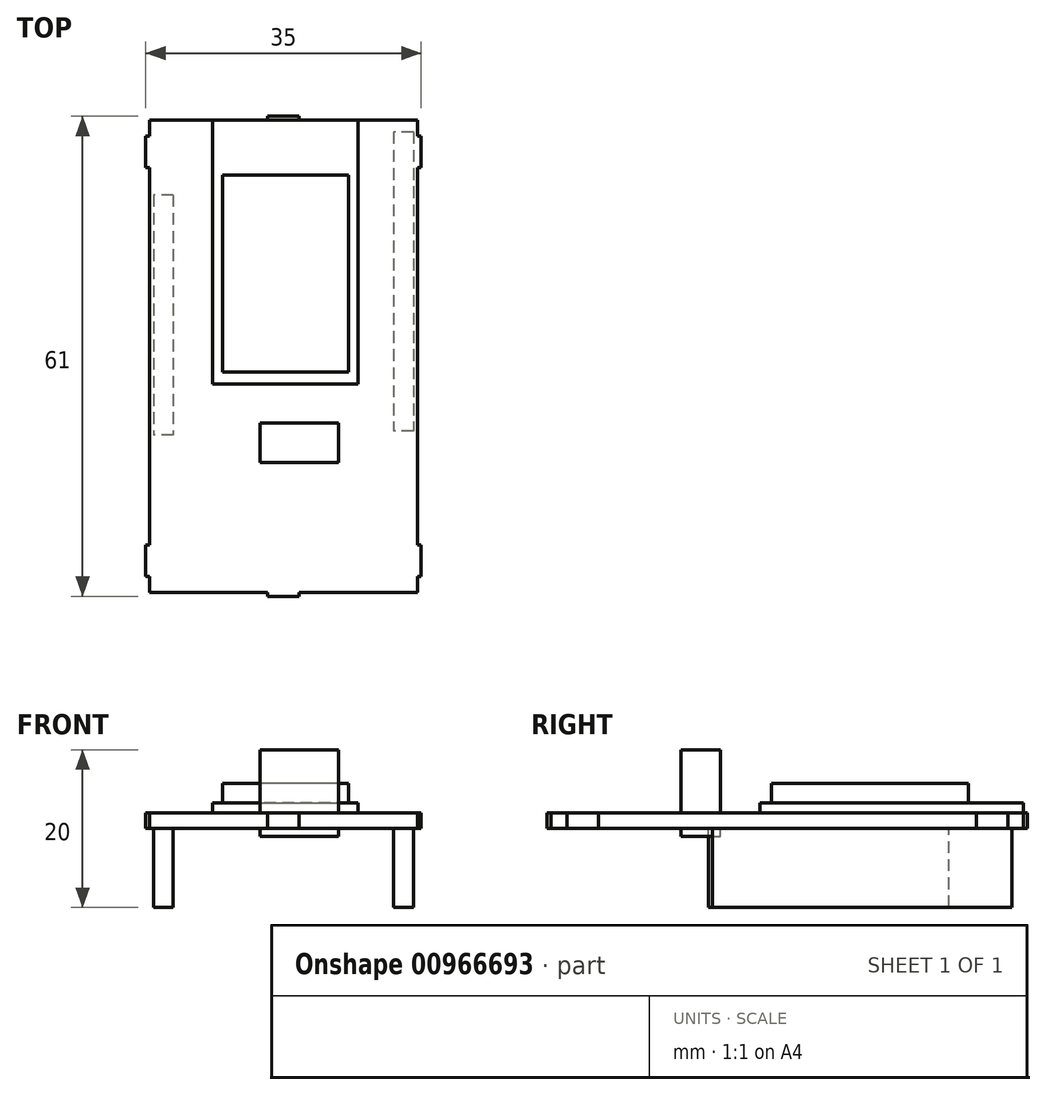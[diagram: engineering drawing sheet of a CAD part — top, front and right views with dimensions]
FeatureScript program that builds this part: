
annotation { "Feature Type Name" : "Feature", "Feature Type Description" : "" }
export const myFeature = defineFeature(function(context is Context, id is Id, definition is map)
    precondition{}
    {
        {
            var Q0;
            Q0=qCreatedBy(makeId("Top.planeOp"),FACE);
            var sketch = newSketch(context, id + "F0", { "sketchPlane" : qUnion([Q0])});
            skLineSegment(sketch, "E0.bottom", {"start": v(17, -30) * mm, "end": v(-17, -30) * mm});
            skLineSegment(sketch, "E0.top", {"start": v(17, 30) * mm, "end": v(-17, 30) * mm});
            skLineSegment(sketch, "E0.left", {"start": v(17, -30) * mm, "end": v(17, 30) * mm});
            skLineSegment(sketch, "E0.right", {"start": v(-17, -30) * mm, "end": v(-17, 30) * mm});
            skPoint(sketch, "E0.middle", {"position": v(0, 0) * mm});
            skLineSegment(sketch, "E1.bottom", {"start": v(2, 30) * mm, "end": v(-2, 30) * mm});
            skLineSegment(sketch, "E1.top", {"start": v(2, 30.5) * mm, "end": v(-2, 30.5) * mm});
            skLineSegment(sketch, "E1.left", {"start": v(2, 30) * mm, "end": v(2, 30.5) * mm});
            skLineSegment(sketch, "E1.right", {"start": v(-2, 30) * mm, "end": v(-2, 30.5) * mm});
            skPoint(sketch, "E1.middle", {"position": v(0, 30.25) * mm});
            skLineSegment(sketch, "E2", {"start": v(17, 30) * mm, "end": v(17, 28) * mm, "construction": true});
            skLineSegment(sketch, "E3.bottom", {"start": v(17, 28) * mm, "end": v(17.5, 28) * mm});
            skLineSegment(sketch, "E3.top", {"start": v(17, 24) * mm, "end": v(17.5, 24) * mm});
            skLineSegment(sketch, "E3.left", {"start": v(17, 28) * mm, "end": v(17, 24) * mm});
            skLineSegment(sketch, "E3.right", {"start": v(17.5, 28) * mm, "end": v(17.5, 24) * mm});
            skLineSegment(sketch, "E4.bottom", {"start": v(-17.5, -24) * mm, "end": v(-17, -24) * mm});
            skLineSegment(sketch, "E4.top", {"start": v(-17.5, -28) * mm, "end": v(-17, -28) * mm});
            skLineSegment(sketch, "E4.left", {"start": v(-17.5, -24) * mm, "end": v(-17.5, -28) * mm});
            skLineSegment(sketch, "E4.right", {"start": v(-17, -24) * mm, "end": v(-17, -28) * mm});
            skLineSegment(sketch, "E5.bottom", {"start": v(17, -24) * mm, "end": v(17.5, -24) * mm});
            skLineSegment(sketch, "E5.top", {"start": v(17, -28) * mm, "end": v(17.5, -28) * mm});
            skLineSegment(sketch, "E5.left", {"start": v(17, -24) * mm, "end": v(17, -28) * mm});
            skLineSegment(sketch, "E5.right", {"start": v(17.5, -24) * mm, "end": v(17.5, -28) * mm});
            skLineSegment(sketch, "E6.bottom", {"start": v(-17.5, 28) * mm, "end": v(-17, 28) * mm});
            skLineSegment(sketch, "E6.top", {"start": v(-17.5, 24) * mm, "end": v(-17, 24) * mm});
            skLineSegment(sketch, "E6.left", {"start": v(-17.5, 28) * mm, "end": v(-17.5, 24) * mm});
            skLineSegment(sketch, "E6.right", {"start": v(-17, 28) * mm, "end": v(-17, 24) * mm});
            skLineSegment(sketch, "E7", {"start": v(-17, -30) * mm, "end": v(-17, -28) * mm, "construction": true});
            skLineSegment(sketch, "E8.bottom", {"start": v(2, -30.5) * mm, "end": v(-2, -30.5) * mm});
            skLineSegment(sketch, "E8.top", {"start": v(2, -30) * mm, "end": v(-2, -30) * mm});
            skLineSegment(sketch, "E8.left", {"start": v(2, -30.5) * mm, "end": v(2, -30) * mm});
            skLineSegment(sketch, "E8.right", {"start": v(-2, -30.5) * mm, "end": v(-2, -30) * mm});
            skPoint(sketch, "E8.middle", {"position": v(0, -30.25) * mm});
            skSolve(sketch);
        }
        {
            var Q0;
            Q0 = qSketchRegion(id + "F0", true);
            extrude(context, id + "F1", {"entities" : qUnion([Q0]), "depth" : 2 * mm, "offsetDistance" : 25 * mm});
        }
        {
            var Q0;
            Q0=makeQuery(id+"F1.opExtrude","CAP_FACE",FACE,{"disambiguationData":[OSD([sQuery(id+"F0.wireOp",EDGE,"E0.bottom"),sQuery(id+"F0.wireOp",EDGE,"E0.top"),sQuery(id+"F0.wireOp",EDGE,"E0.left"),sQuery(id+"F0.wireOp",EDGE,"E0.right"),sQuery(id+"F0.wireOp",EDGE,"E1.top"),sQuery(id+"F0.wireOp",EDGE,"E1.left"),sQuery(id+"F0.wireOp",EDGE,"E1.right"),sQuery(id+"F0.wireOp",EDGE,"E3.bottom"),sQuery(id+"F0.wireOp",EDGE,"E3.top"),sQuery(id+"F0.wireOp",EDGE,"E3.right"),sQuery(id+"F0.wireOp",EDGE,"E4.bottom"),sQuery(id+"F0.wireOp",EDGE,"E4.top"),sQuery(id+"F0.wireOp",EDGE,"E4.left"),sQuery(id+"F0.wireOp",EDGE,"E5.bottom"),sQuery(id+"F0.wireOp",EDGE,"E5.top"),sQuery(id+"F0.wireOp",EDGE,"E5.right"),sQuery(id+"F0.wireOp",EDGE,"E6.bottom"),sQuery(id+"F0.wireOp",EDGE,"E6.top"),sQuery(id+"F0.wireOp",EDGE,"E6.left"),sQuery(id+"F0.wireOp",EDGE,"E8.bottom"),sQuery(id+"F0.wireOp",EDGE,"E8.left"),sQuery(id+"F0.wireOp",EDGE,"E8.right")])],"isStart":false});
            var sketch = newSketch(context, id + "F2", { "sketchPlane" : qUnion([Q0])});
            skLineSegment(sketch, "E9", {"start": v(9.5, 30) * mm, "end": v(17, 30) * mm, "construction": true});
            skLineSegment(sketch, "E10.bottom", {"start": v(-9, 30) * mm, "end": v(9.5, 30) * mm});
            skLineSegment(sketch, "E10.top", {"start": v(-9, -3.5) * mm, "end": v(9.5, -3.5) * mm});
            skLineSegment(sketch, "E10.left", {"start": v(-9, 30) * mm, "end": v(-9, -3.5) * mm});
            skLineSegment(sketch, "E10.right", {"start": v(9.5, 30) * mm, "end": v(9.5, -3.5) * mm});
            skSolve(sketch);
        }
        {
            var Q0;
            Q0 = qSketchRegion(id + "F2", true);
            extrude(context, id + "F3", {"entities" : qUnion([Q0]), "depth" : 1.27 * mm, "offsetDistance" : 25 * mm});
        }
        {
            var Q0;
            Q0=makeQuery(id+"F3.opExtrude","CAP_FACE",FACE,{"disambiguationData":[OSD([sQuery(id+"F2.wireOp",EDGE,"E10.bottom"),sQuery(id+"F2.wireOp",EDGE,"E10.top"),sQuery(id+"F2.wireOp",EDGE,"E10.left"),sQuery(id+"F2.wireOp",EDGE,"E10.right")])],"isStart":false});
            var sketch = newSketch(context, id + "F4", { "sketchPlane" : qUnion([Q0])});
            skLineSegment(sketch, "E11.bottom", {"start": v(8.25, 23) * mm, "end": v(-7.75, 23) * mm});
            skLineSegment(sketch, "E11.top", {"start": v(8.25, -2) * mm, "end": v(-7.75, -2) * mm});
            skLineSegment(sketch, "E11.left", {"start": v(8.25, 23) * mm, "end": v(8.25, -2) * mm});
            skLineSegment(sketch, "E11.right", {"start": v(-7.75, 23) * mm, "end": v(-7.75, -2) * mm});
            skPoint(sketch, "E11.middle", {"position": v(0.25, 10.5) * mm});
            skLineSegment(sketch, "E12", {"start": v(0.25, 23) * mm, "end": v(0.25, 30) * mm, "construction": true});
            skSolve(sketch);
        }
        {
            var Q0;
            Q0 = qSketchRegion(id + "F4", true);
            extrude(context, id + "F5", {"entities" : qUnion([Q0]), "depth" : 2.5 * mm, "offsetDistance" : 25 * mm});
        }
        {
            var Q0;
            Q0=makeQuery(id+"F1.opExtrude","CAP_FACE",FACE,{"disambiguationData":[OSD([sQuery(id+"F0.wireOp",EDGE,"E0.bottom"),sQuery(id+"F0.wireOp",EDGE,"E0.top"),sQuery(id+"F0.wireOp",EDGE,"E0.left"),sQuery(id+"F0.wireOp",EDGE,"E0.right"),sQuery(id+"F0.wireOp",EDGE,"E1.top"),sQuery(id+"F0.wireOp",EDGE,"E1.left"),sQuery(id+"F0.wireOp",EDGE,"E1.right"),sQuery(id+"F0.wireOp",EDGE,"E3.bottom"),sQuery(id+"F0.wireOp",EDGE,"E3.top"),sQuery(id+"F0.wireOp",EDGE,"E3.right"),sQuery(id+"F0.wireOp",EDGE,"E4.bottom"),sQuery(id+"F0.wireOp",EDGE,"E4.top"),sQuery(id+"F0.wireOp",EDGE,"E4.left"),sQuery(id+"F0.wireOp",EDGE,"E5.bottom"),sQuery(id+"F0.wireOp",EDGE,"E5.top"),sQuery(id+"F0.wireOp",EDGE,"E5.right"),sQuery(id+"F0.wireOp",EDGE,"E6.bottom"),sQuery(id+"F0.wireOp",EDGE,"E6.top"),sQuery(id+"F0.wireOp",EDGE,"E6.left"),sQuery(id+"F0.wireOp",EDGE,"E8.bottom"),sQuery(id+"F0.wireOp",EDGE,"E8.left"),sQuery(id+"F0.wireOp",EDGE,"E8.right")])],"isStart":false});
            var sketch = newSketch(context, id + "F6", { "sketchPlane" : qUnion([Q0])});
            skLineSegment(sketch, "E13.bottom", {"start": v(-3, -13.5) * mm, "end": v(7, -13.5) * mm});
            skLineSegment(sketch, "E13.top", {"start": v(-3, -8.5) * mm, "end": v(7, -8.5) * mm});
            skLineSegment(sketch, "E13.left", {"start": v(-3, -13.5) * mm, "end": v(-3, -8.5) * mm});
            skLineSegment(sketch, "E13.right", {"start": v(7, -13.5) * mm, "end": v(7, -8.5) * mm});
            skLineSegment(sketch, "E14", {"start": v(7, -8.5) * mm, "end": v(17, -8.5) * mm, "construction": true});
            skLineSegment(sketch, "E15", {"start": v(7, -8.5) * mm, "end": v(7, -3.5) * mm, "construction": true});
            skLineSegment(sketch, "E16", {"start": v(-5.02, -9.59) * mm, "end": v(-5.02, -5.08) * mm});
            skSolve(sketch);
        }
        {
            var Q0;
            Q0 = qSketchRegion(id + "F6", true);
            extrude(context, id + "F7", {"entities" : qUnion([Q0]), "depth" : 8 * mm, "offsetDistance" : 25 * mm});
        }
        {
            var Q0;
            Q0=makeQuery(id+"F1.opExtrude","CAP_FACE",FACE,{"disambiguationData":[OSD([sQuery(id+"F0.wireOp",EDGE,"E0.bottom"),sQuery(id+"F0.wireOp",EDGE,"E0.top"),sQuery(id+"F0.wireOp",EDGE,"E0.left"),sQuery(id+"F0.wireOp",EDGE,"E0.right"),sQuery(id+"F0.wireOp",EDGE,"E1.top"),sQuery(id+"F0.wireOp",EDGE,"E1.left"),sQuery(id+"F0.wireOp",EDGE,"E1.right"),sQuery(id+"F0.wireOp",EDGE,"E3.bottom"),sQuery(id+"F0.wireOp",EDGE,"E3.top"),sQuery(id+"F0.wireOp",EDGE,"E3.right"),sQuery(id+"F0.wireOp",EDGE,"E4.bottom"),sQuery(id+"F0.wireOp",EDGE,"E4.top"),sQuery(id+"F0.wireOp",EDGE,"E4.left"),sQuery(id+"F0.wireOp",EDGE,"E5.bottom"),sQuery(id+"F0.wireOp",EDGE,"E5.top"),sQuery(id+"F0.wireOp",EDGE,"E5.right"),sQuery(id+"F0.wireOp",EDGE,"E6.bottom"),sQuery(id+"F0.wireOp",EDGE,"E6.top"),sQuery(id+"F0.wireOp",EDGE,"E6.left"),sQuery(id+"F0.wireOp",EDGE,"E8.bottom"),sQuery(id+"F0.wireOp",EDGE,"E8.left"),sQuery(id+"F0.wireOp",EDGE,"E8.right")])],"isStart":true});
            var sketch = newSketch(context, id + "F8", { "sketchPlane" : qUnion([Q0])});
            skLineSegment(sketch, "E17.bottom", {"start": v(-3, 13.5) * mm, "end": v(7, 13.5) * mm});
            skLineSegment(sketch, "E17.top", {"start": v(-3, 8.5) * mm, "end": v(7, 8.5) * mm});
            skLineSegment(sketch, "E17.left", {"start": v(-3, 13.5) * mm, "end": v(-3, 8.5) * mm});
            skLineSegment(sketch, "E17.right", {"start": v(7, 13.5) * mm, "end": v(7, 8.5) * mm});
            skSolve(sketch);
        }
        {
            var Q0;
            Q0 = qSketchRegion(id + "F8", true);
            extrude(context, id + "F9", {"entities" : qUnion([Q0]), "depth" : 1 * mm, "offsetDistance" : 25 * mm});
        }
        {
            var Q0;
            Q0=makeQuery(id+"F1.opExtrude","CAP_FACE",FACE,{"disambiguationData":[OSD([sQuery(id+"F0.wireOp",EDGE,"E0.bottom"),sQuery(id+"F0.wireOp",EDGE,"E0.top"),sQuery(id+"F0.wireOp",EDGE,"E0.left"),sQuery(id+"F0.wireOp",EDGE,"E0.right"),sQuery(id+"F0.wireOp",EDGE,"E1.top"),sQuery(id+"F0.wireOp",EDGE,"E1.left"),sQuery(id+"F0.wireOp",EDGE,"E1.right"),sQuery(id+"F0.wireOp",EDGE,"E3.bottom"),sQuery(id+"F0.wireOp",EDGE,"E3.top"),sQuery(id+"F0.wireOp",EDGE,"E3.right"),sQuery(id+"F0.wireOp",EDGE,"E4.bottom"),sQuery(id+"F0.wireOp",EDGE,"E4.top"),sQuery(id+"F0.wireOp",EDGE,"E4.left"),sQuery(id+"F0.wireOp",EDGE,"E5.bottom"),sQuery(id+"F0.wireOp",EDGE,"E5.top"),sQuery(id+"F0.wireOp",EDGE,"E5.right"),sQuery(id+"F0.wireOp",EDGE,"E6.bottom"),sQuery(id+"F0.wireOp",EDGE,"E6.top"),sQuery(id+"F0.wireOp",EDGE,"E6.left"),sQuery(id+"F0.wireOp",EDGE,"E8.bottom"),sQuery(id+"F0.wireOp",EDGE,"E8.left"),sQuery(id+"F0.wireOp",EDGE,"E8.right")])],"isStart":true});
            var sketch = newSketch(context, id + "F10", { "sketchPlane" : qUnion([Q0])});
            skLineSegment(sketch, "E18", {"start": v(17, -30) * mm, "end": v(17, -28.5) * mm, "construction": true});
            skLineSegment(sketch, "E19", {"start": v(-17, -30) * mm, "end": v(-17, -20.5) * mm, "construction": true});
            skLineSegment(sketch, "E20.bottom", {"start": v(-14, -20.5) * mm, "end": v(-16.5, -20.5) * mm});
            skLineSegment(sketch, "E20.top", {"start": v(-14, 10) * mm, "end": v(-16.5, 10) * mm});
            skLineSegment(sketch, "E20.left", {"start": v(-14, -20.5) * mm, "end": v(-14, 10) * mm});
            skLineSegment(sketch, "E20.right", {"start": v(-16.5, -20.5) * mm, "end": v(-16.5, 10) * mm});
            skLineSegment(sketch, "E21", {"start": v(17, -28.5) * mm, "end": v(16.5, -28.5) * mm, "construction": true});
            skLineSegment(sketch, "E22.bottom", {"start": v(16.5, -28.5) * mm, "end": v(14, -28.5) * mm});
            skLineSegment(sketch, "E22.top", {"start": v(16.5, 9.5) * mm, "end": v(14, 9.5) * mm});
            skLineSegment(sketch, "E22.left", {"start": v(16.5, -28.5) * mm, "end": v(16.5, 9.5) * mm});
            skLineSegment(sketch, "E22.right", {"start": v(14, -28.5) * mm, "end": v(14, 9.5) * mm});
            skLineSegment(sketch, "E23", {"start": v(-16.5, -20.5) * mm, "end": v(-17, -20.5) * mm, "construction": true});
            skSolve(sketch);
        }
        {
            var Q0;
            Q0 = qSketchRegion(id + "F10", true);
            extrude(context, id + "F11", {"entities" : qUnion([Q0]), "depth" : 10 * mm, "offsetDistance" : 25 * mm});
        }
    });
